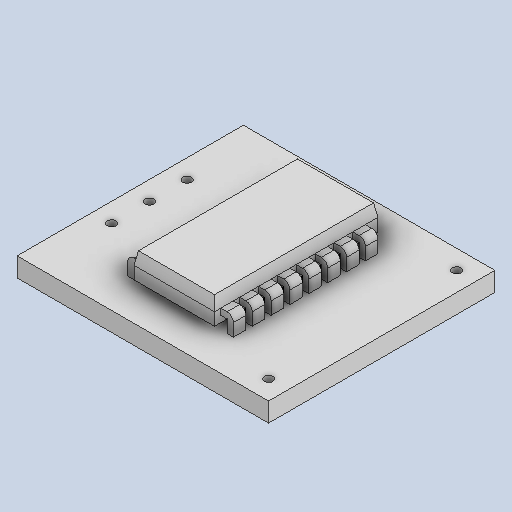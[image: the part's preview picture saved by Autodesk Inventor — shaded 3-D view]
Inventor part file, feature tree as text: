
AUTODESK INVENTOR PART (.ipt)
format: ipt  version: 2025.2 (Build 292293000, 293)  size: 181,760 bytes
history: native  units: mm
features: other x1, mirror x1
ambient origin geometry x8: Origin, YZ Plane, XZ Plane, XY Plane, X Axis, Y Axis, Z Axis, Center Point
bodies: Body1 (feature_tree)
feature tree (2):
  other  "Bryła1"
  mirror  "Mirror1"
